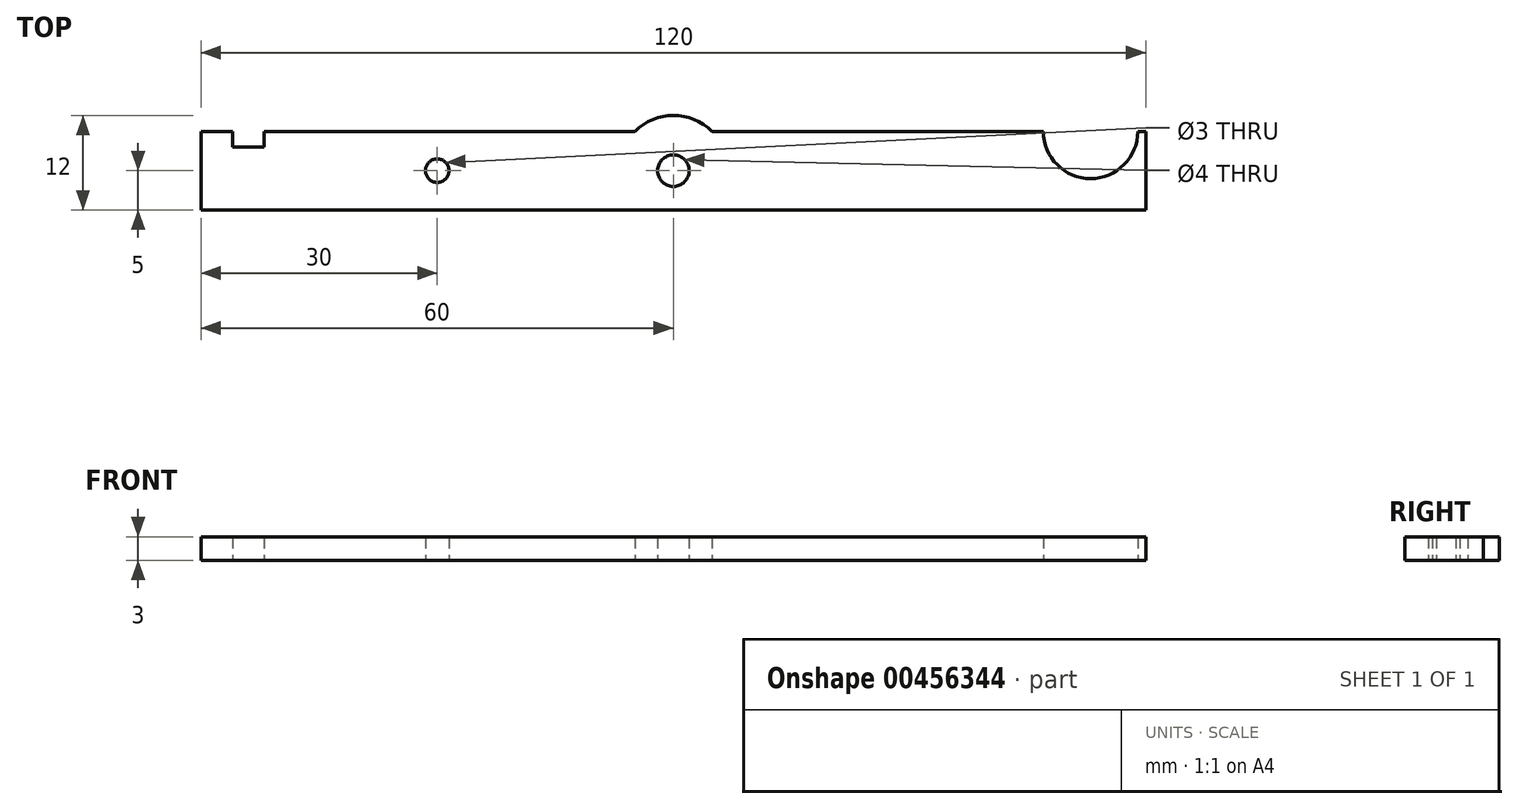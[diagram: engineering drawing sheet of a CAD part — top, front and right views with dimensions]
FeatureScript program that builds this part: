
annotation { "Feature Type Name" : "Feature", "Feature Type Description" : "" }
export const myFeature = defineFeature(function(context is Context, id is Id, definition is map)
    precondition{}
    {
        {
            var Q0;
            Q0=qCreatedBy(makeId("Top.planeOp"),FACE);
            var sketch = newSketch(context, id + "F0", { "sketchPlane" : qUnion([Q0])});
            skLineSegment(sketch, "E0.bottom", {"start": v(-60, 5) * mm, "end": v(60, 5) * mm});
            skLineSegment(sketch, "E0.top", {"start": v(-60, -5) * mm, "end": v(60, -5) * mm});
            skLineSegment(sketch, "E0.left", {"start": v(-60, 5) * mm, "end": v(-60, -5) * mm});
            skLineSegment(sketch, "E0.right", {"start": v(60, 5) * mm, "end": v(60, -5) * mm});
            skPoint(sketch, "E0.middle", {"position": v(0, 0) * mm});
            skLineSegment(sketch, "E1.bottom", {"start": v(-56, 5) * mm, "end": v(-52, 5) * mm});
            skLineSegment(sketch, "E1.top", {"start": v(-56, 3) * mm, "end": v(-52, 3) * mm});
            skLineSegment(sketch, "E1.left", {"start": v(-56, 5) * mm, "end": v(-56, 3) * mm});
            skLineSegment(sketch, "E1.right", {"start": v(-52, 5) * mm, "end": v(-52, 3) * mm});
            skCircle(sketch, "E2", {"center": v(0, 0) * mm, "radius": 2 * mm});
            skCircle(sketch, "E3", {"center": v(0, 0) * mm, "radius": 7 * mm});
            skCircle(sketch, "E4", {"center": v(-30, 0) * mm, "radius": 1.5 * mm});
            skCircle(sketch, "E5", {"center": v(53, 5) * mm, "radius": 6 * mm});
            skSolve(sketch);
        }
        {
            var Q0;
            {var subQ0=sQuery(id+"F0.wireOp",EDGE,"E0.left");Q0=makeQuery(id+"F0.imprint","IMPRINT",FACE,{"disambiguationData":[TD([[makeQuery(id+"F0.imprint","IMPRINT",EDGE,{"derivedFrom":subQ0}),1.0]])]});}
            var Q1;
            Q1=makeQuery(id+"F0.imprint","IMPRINT",FACE,{"disambiguationData":[TD([[makeQuery(id+"F0.imprint","IMPRINT",EDGE,{"derivedFrom":sQuery(id+"F0.wireOp",EDGE,"E2")}),-1.0]])]});
            var Q2;
            {var subQ0=sQuery(id+"F0.wireOp",EDGE,"E3");var subQ1=sQuery(id+"F0.wireOp",EDGE,"E0.top");var subQ2=makeQuery(id+"F0.imprint","INTERSECT",VERTEX,{"disambiguationData":[OD(0.0)],"derivedFrom":[subQ1,subQ0]});Q2=makeQuery(id+"F0.imprint","IMPRINT",FACE,{"disambiguationData":[TD([[makeQuery(id+"F0.imprint","IMPRINT",EDGE,{"disambiguationData":[TD([[subQ2,-1.0]])],"derivedFrom":subQ1}),-1.0]])]});}
            var Q3;
            {var subQ0=sQuery(id+"F0.wireOp",EDGE,"E3");var subQ1=sQuery(id+"F0.wireOp",EDGE,"E0.bottom");var subQ2=makeQuery(id+"F0.imprint","INTERSECT",VERTEX,{"disambiguationData":[OD(0.0)],"derivedFrom":[subQ1,subQ0]});Q3=makeQuery(id+"F0.imprint","IMPRINT",FACE,{"disambiguationData":[TD([[makeQuery(id+"F0.imprint","IMPRINT",EDGE,{"disambiguationData":[TD([[subQ2,-1.0]])],"derivedFrom":subQ1}),1.0]])]});}
            var Q4;
            {var subQ0=sQuery(id+"F0.wireOp",EDGE,"E0.right");Q4=makeQuery(id+"F0.imprint","IMPRINT",FACE,{"disambiguationData":[TD([[makeQuery(id+"F0.imprint","IMPRINT",EDGE,{"derivedFrom":subQ0}),-1.0]])]});}
            extrude(context, id + "F1", {"entities" : qUnion([Q0, Q1, Q2, Q3, Q4]), "depth" : 3 * mm});
        }
    });
